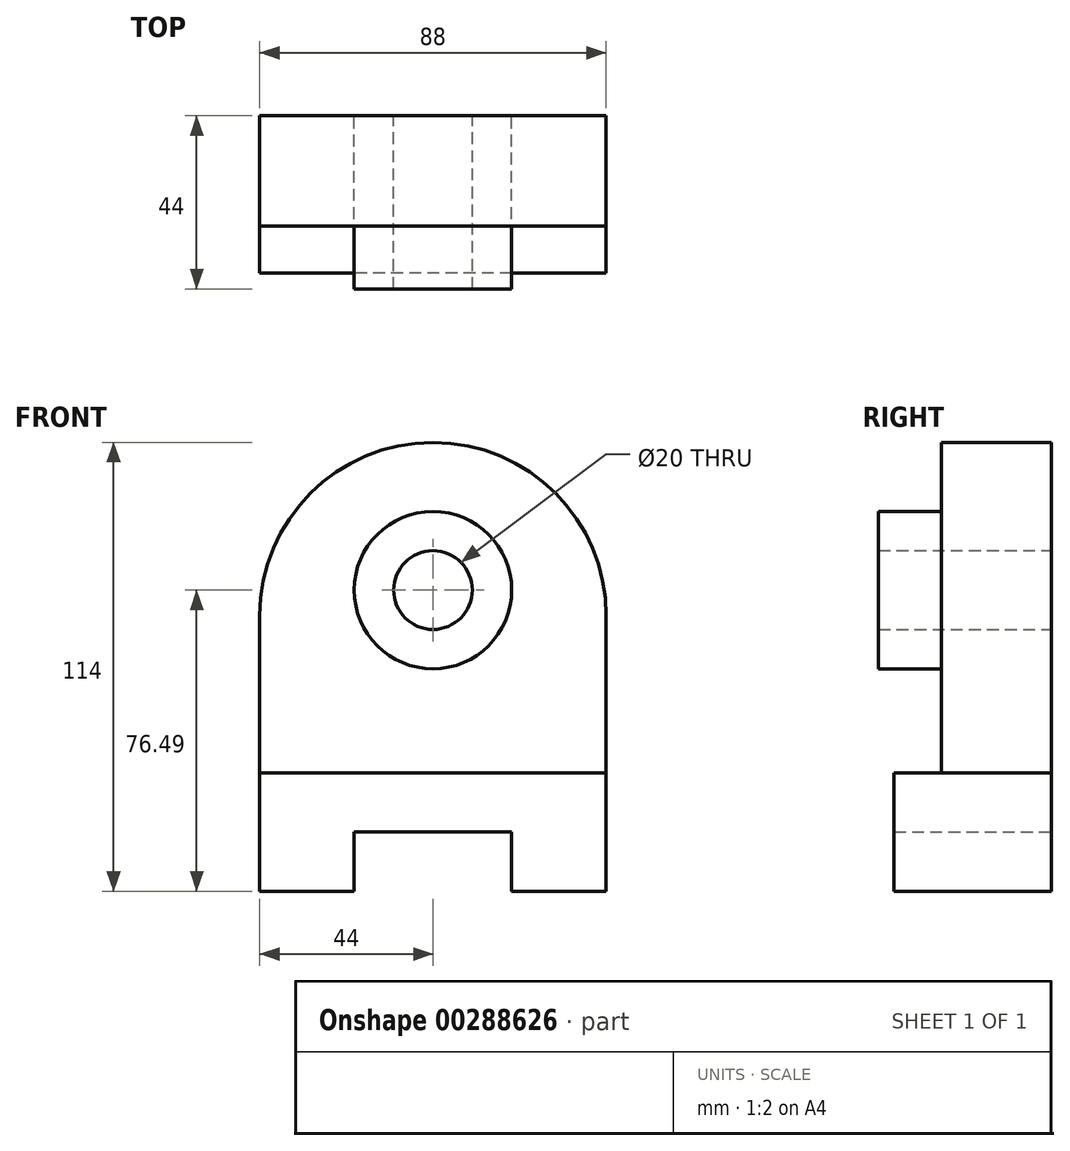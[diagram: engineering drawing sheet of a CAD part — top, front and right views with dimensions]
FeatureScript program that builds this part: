
annotation { "Feature Type Name" : "Feature", "Feature Type Description" : "" }
export const myFeature = defineFeature(function(context is Context, id is Id, definition is map)
    precondition{}
    {
        {
            var Q0;
            Q0=qCreatedBy(makeId("Front.planeOp"),FACE);
            var sketch = newSketch(context, id + "F0", { "sketchPlane" : qUnion([Q0])});
            skLineSegment(sketch, "E0", {"start": v(-44, -10.5) * mm, "end": v(-44, -40.5) * mm});
            skLineSegment(sketch, "E1", {"start": v(-44, -40.5) * mm, "end": v(-20, -40.5) * mm});
            skLineSegment(sketch, "E2", {"start": v(44, -40.5) * mm, "end": v(44, -10.5) * mm});
            skLineSegment(sketch, "E3", {"start": v(44, -10.5) * mm, "end": v(-44, -10.5) * mm});
            skLineSegment(sketch, "E4", {"start": v(-20, -40.5) * mm, "end": v(-20, -25.5) * mm});
            skLineSegment(sketch, "E5", {"start": v(-20, -25.5) * mm, "end": v(20, -25.5) * mm});
            skLineSegment(sketch, "E6", {"start": v(20, -25.5) * mm, "end": v(20, -40.5) * mm});
            skLineSegment(sketch, "E7.trimOffspring", {"start": v(20, -40.5) * mm, "end": v(44, -40.5) * mm});
            skSolve(sketch);
        }
        {
            var Q0;
            Q0=makeQuery(id+"F0.imprint","IMPRINT",FACE,{"disambiguationData":[TD([[makeQuery(id+"F0.imprint","IMPRINT",EDGE,{"derivedFrom":sQuery(id+"F0.wireOp",EDGE,"E0")}),1.0]])]});
            extrude(context, id + "F1", {"entities" : qUnion([Q0]), "depth" : 40 * mm});
        }
        {
            var Q0;
            Q0=qCreatedBy(makeId("Front.planeOp"),FACE);
            var sketch = newSketch(context, id + "F2", { "sketchPlane" : qUnion([Q0])});
            skLineSegment(sketch, "E8", {"start": v(44, -10.5) * mm, "end": v(44, 29.5) * mm});
            skLineSegment(sketch, "E9", {"start": v(-44, 29.5) * mm, "end": v(-44, -10.5) * mm});
            skLineSegment(sketch, "E10", {"start": v(-44, -10.5) * mm, "end": v(44, -10.5) * mm});
            skArc(sketch, "E11", {"start": v(44, 29.5) * mm, "mid": v(0, 73.5) * mm, "end": v(-44, 29.5) * mm});
            skSolve(sketch);
        }
        {
            var Q0;
            Q0 = qSketchRegion(id + "F2", true);
            extrude(context, id + "F3", {"entities" : qUnion([Q0]), "depth" : 28 * mm});
        }
        {
            var Q0;
            Q0=makeQuery(id+"F3.opExtrude","CAP_FACE",FACE,{"disambiguationData":[OSD([sQuery(id+"F2.wireOp",EDGE,"E8"),sQuery(id+"F2.wireOp",EDGE,"E9"),sQuery(id+"F2.wireOp",EDGE,"E10"),sQuery(id+"F2.wireOp",EDGE,"E11")])],"isStart":false});
            var sketch = newSketch(context, id + "F4", { "sketchPlane" : qUnion([Q0])});
            skCircle(sketch, "E12", {"center": v(0, 36) * mm, "radius": 20 * mm});
            skCircle(sketch, "E13", {"center": v(0, 36) * mm, "radius": 10 * mm});
            skSolve(sketch);
        }
        {
            var Q0;
            Q0=makeQuery(id+"F4.imprint","IMPRINT",FACE,{"disambiguationData":[TD([[makeQuery(id+"F4.imprint","IMPRINT",EDGE,{"derivedFrom":sQuery(id+"F4.wireOp",EDGE,"E12")}),1.0]])]});
            extrude(context, id + "F5", {"entities" : qUnion([Q0]), "operationType" : NewBodyOperationType.ADD, "depth" : 16 * mm});
        }
        {
            var Q0;
            Q0=makeQuery(id+"F5.boolean.opBoolean","SPLIT",FACE,{"disambiguationData":[TD([makeQuery(id+"F5.opExtrude","SWEPT_FACE",FACE,{"disambiguationData":[OSD([sQuery(id+"F4.wireOp",EDGE,"E13")])]})])],"derivedFrom":makeQuery(id+"F3.opExtrude","CAP_FACE",FACE,{"disambiguationData":[OSD([sQuery(id+"F2.wireOp",EDGE,"E8"),sQuery(id+"F2.wireOp",EDGE,"E9"),sQuery(id+"F2.wireOp",EDGE,"E10"),sQuery(id+"F2.wireOp",EDGE,"E11")])],"isStart":false})});
            extrude(context, id + "F6", {"entities" : qUnion([Q0]), "operationType" : NewBodyOperationType.REMOVE, "oppositeDirection" : true, "depth" : 100 * mm});
        }
    });
